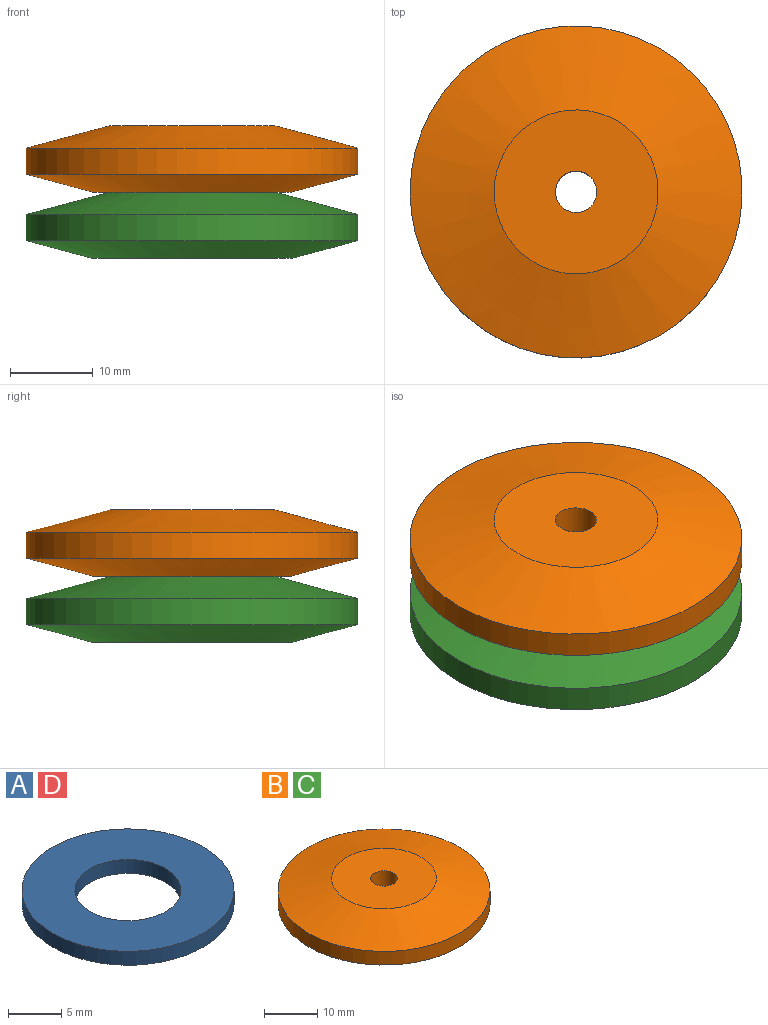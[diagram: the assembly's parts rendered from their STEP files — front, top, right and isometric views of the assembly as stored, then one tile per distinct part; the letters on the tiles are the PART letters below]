
ASSEMBLY  parts=4 mates=3
PART A: 4 faces, bbox 20x20x1.6 mm
  f0: plane 20x20mm, normal (0,0,1), area 235.6mm2, adj f1,f3
  f1: cylinder r=5mm len=10mm, axis (0,0,-1), area 50.3mm2, adj f0,f2
  f2: plane 20x20mm, normal (0,0,-1), area 235.6mm2, adj f1,f3
  f3: cylinder r=10mm len=20mm, axis (0,0,-1), area 100.5mm2, adj f0,f2
PART B: 10 faces, bbox 40x40x8 mm
  f0: cone r=20mm half-angle=75deg, axis (0,0,-1), area 983.6mm2, adj f1,f8
  f1: plane 19.76x19.76mm, normal (0,0,1), area 286.9mm2, adj f0,f9
  f2: plane 10x10mm, normal (0,0,-1), area 58.9mm2, adj f3,f9
  f3: cylinder r=5mm len=10mm, axis (0,0,-1), area 50.3mm2, adj f2,f4
  f4: plane 20x20mm, normal (0,0,-1), area 235.6mm2, adj f3,f5
  f5: cylinder r=10mm len=20mm, axis (0,0,-1), area 100.5mm2, adj f4,f6
  f6: plane 24x24mm, normal (0,0,-1), area 138.2mm2, adj f5,f7
  f7: cone r=12mm half-angle=75deg, axis (0,0,1), area 832.6mm2, adj f6,f8
  f8: cylinder r=20mm len=40mm, axis (0,0,-1), area 395.1mm2, adj f0,f7
  f9: cylinder r=2.5mm len=8mm, axis (0,0,1), area 125.7mm2, adj f1,f2
PART C: same geometry as B
PART D: same geometry as A
PLACE A t=(5.49,8.48,9.51)mm
PLACE B t=(5.49,8.48,9.51)mm
PLACE C t=(5.49,8.48,1.51)mm
PLACE D t=(5.49,8.48,1.51)mm
MATE fastened D.f1 <-> C.f0  axis (0,0,-1) through (5.49,8.48,3.11)mm
MATE fastened A.f1 <-> B.f0  axis (0,0,-1) through (5.49,8.48,11.11)mm
MATE fastened C.f0 <-> B.f0  axis (0,0,1) through (5.49,8.48,9.51)mm
